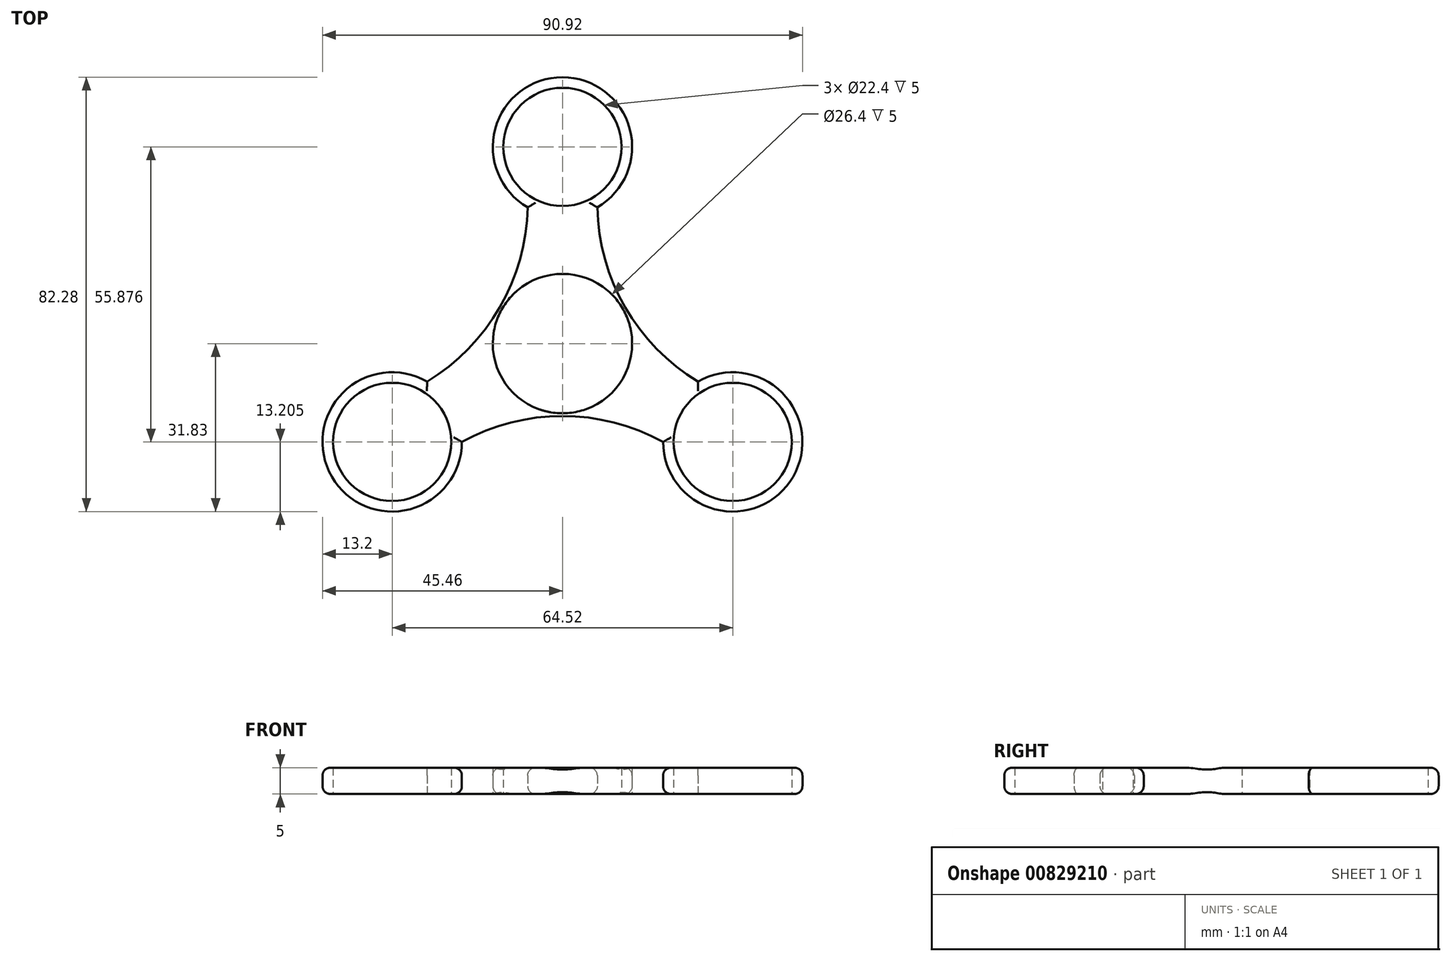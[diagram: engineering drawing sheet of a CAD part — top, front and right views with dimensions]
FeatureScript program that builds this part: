
annotation { "Feature Type Name" : "Feature", "Feature Type Description" : "" }
export const myFeature = defineFeature(function(context is Context, id is Id, definition is map)
    precondition{}
    {
        {
            var Q0;
            Q0=qCreatedBy(makeId("Top.planeOp"),FACE);
            var sketch = newSketch(context, id + "F0", { "sketchPlane" : qUnion([Q0])});
            skCircle(sketch, "E0", {"center": v(0, 0) * mm, "radius": 11.2 * mm});
            skCircle(sketch, "E1", {"center": v(0, 0) * mm, "radius": 13.2 * mm});
            skCircle(sketch, "E2", {"center": v(0, 37.25) * mm, "radius": 11.2 * mm});
            skArc(sketch, "E3", {"start": v(6.6, 25.82) * mm, "mid": v(0, 50.45) * mm, "end": v(-6.6, 25.82) * mm});
            skArc(sketch, "E4.1.0", {"start": v(-25.66, -7.2) * mm, "mid": v(-43.7, -25.23) * mm, "end": v(-19.06, -18.63) * mm});
            skCircle(sketch, "E4.1.1", {"center": v(-32.26, -18.63) * mm, "radius": 11.2 * mm});
            skCircle(sketch, "E4.2.0", {"center": v(32.26, -18.63) * mm, "radius": 13.2 * mm});
            skCircle(sketch, "E4.2.1", {"center": v(32.26, -18.63) * mm, "radius": 11.2 * mm});
            skLineSegment(sketch, "E5", {"start": v(5.6, 27.55) * mm, "end": v(6.6, 25.82) * mm, "construction": true});
            skArc(sketch, "E6", {"start": v(6.6, 25.82) * mm, "mid": v(11.88, 6.86) * mm, "end": v(25.66, -7.2) * mm});
            skArc(sketch, "E7.1.0", {"start": v(-25.66, -7.2) * mm, "mid": v(-11.88, 6.86) * mm, "end": v(-6.6, 25.82) * mm});
            skArc(sketch, "E7.2.0", {"start": v(19.06, -18.63) * mm, "mid": v(0, -13.72) * mm, "end": v(-19.06, -18.63) * mm});
            skLineSegment(sketch, "E8.trimOffspring", {"start": v(-11.43, -6.6) * mm, "end": v(-9.7, -5.6) * mm, "construction": true});
            skLineSegment(sketch, "E9.trimOffspring", {"start": v(9.7, 5.6) * mm, "end": v(11.88, 6.86) * mm, "construction": true});
            skLineSegment(sketch, "E10.trimOffspring", {"start": v(25.66, -7.2) * mm, "end": v(26.66, -8.93) * mm, "construction": true});
            skSolve(sketch);
        }
        {
            var Q0;
            Q0 = qSketchRegion(id + "F0", true);
            extrude(context, id + "F1", {"entities" : qUnion([Q0]), "depth" : 5 * mm, "offsetDistance" : 25 * mm});
        }
        {
            var Q0;
            Q0=makeQuery(id+"F1.opExtrude","CAP_EDGE",EDGE,{"disambiguationData":[OSD([sQuery(id+"F0.wireOp",EDGE,"E4.1.0")])],"isStart":false});
            var Q1;
            Q1=makeQuery(id+"F1.opExtrude","CAP_EDGE",EDGE,{"disambiguationData":[OSD([sQuery(id+"F0.wireOp",EDGE,"E7.2.0")])],"isStart":false});
            var Q2;
            Q2=makeQuery(id+"F1.opExtrude","CAP_EDGE",EDGE,{"disambiguationData":[OSD([sQuery(id+"F0.wireOp",EDGE,"E4.2.0")])],"isStart":false});
            var Q3;
            Q3=makeQuery(id+"F1.opExtrude","CAP_EDGE",EDGE,{"disambiguationData":[OSD([sQuery(id+"F0.wireOp",EDGE,"E6")])],"isStart":false});
            var Q4;
            Q4=makeQuery(id+"F1.opExtrude","CAP_EDGE",EDGE,{"disambiguationData":[OSD([sQuery(id+"F0.wireOp",EDGE,"E3")])],"isStart":false});
            var Q5;
            Q5=makeQuery(id+"F1.opExtrude","CAP_EDGE",EDGE,{"disambiguationData":[OSD([sQuery(id+"F0.wireOp",EDGE,"E7.1.0")])],"isStart":false});
            fillet(context, id + "F2", {"entities" : qUnion([Q0, Q1, Q2, Q3, Q4, Q5]), "radius" : 1.5 * mm, "tangentPropagation" : true, "allowEdgeOverflow" : false});
        }
        {
            var Q0;
            Q0=makeQuery(id+"F1.opExtrude","CAP_EDGE",EDGE,{"disambiguationData":[OSD([sQuery(id+"F0.wireOp",EDGE,"E4.1.0")])],"isStart":true});
            var Q1;
            Q1=makeQuery(id+"F1.opExtrude","CAP_EDGE",EDGE,{"disambiguationData":[OSD([sQuery(id+"F0.wireOp",EDGE,"E7.1.0")])],"isStart":true});
            var Q2;
            Q2=makeQuery(id+"F1.opExtrude","CAP_EDGE",EDGE,{"disambiguationData":[OSD([sQuery(id+"F0.wireOp",EDGE,"E3")])],"isStart":true});
            var Q3;
            Q3=makeQuery(id+"F1.opExtrude","CAP_EDGE",EDGE,{"disambiguationData":[OSD([sQuery(id+"F0.wireOp",EDGE,"E6")])],"isStart":true});
            var Q4;
            Q4=makeQuery(id+"F1.opExtrude","CAP_EDGE",EDGE,{"disambiguationData":[OSD([sQuery(id+"F0.wireOp",EDGE,"E4.2.0")])],"isStart":true});
            var Q5;
            Q5=makeQuery(id+"F1.opExtrude","CAP_EDGE",EDGE,{"disambiguationData":[OSD([sQuery(id+"F0.wireOp",EDGE,"E7.2.0")])],"isStart":true});
            fillet(context, id + "F3", {"entities" : qUnion([Q0, Q1, Q2, Q3, Q4, Q5]), "radius" : 1.5 * mm, "tangentPropagation" : true, "allowEdgeOverflow" : false});
        }
    });
